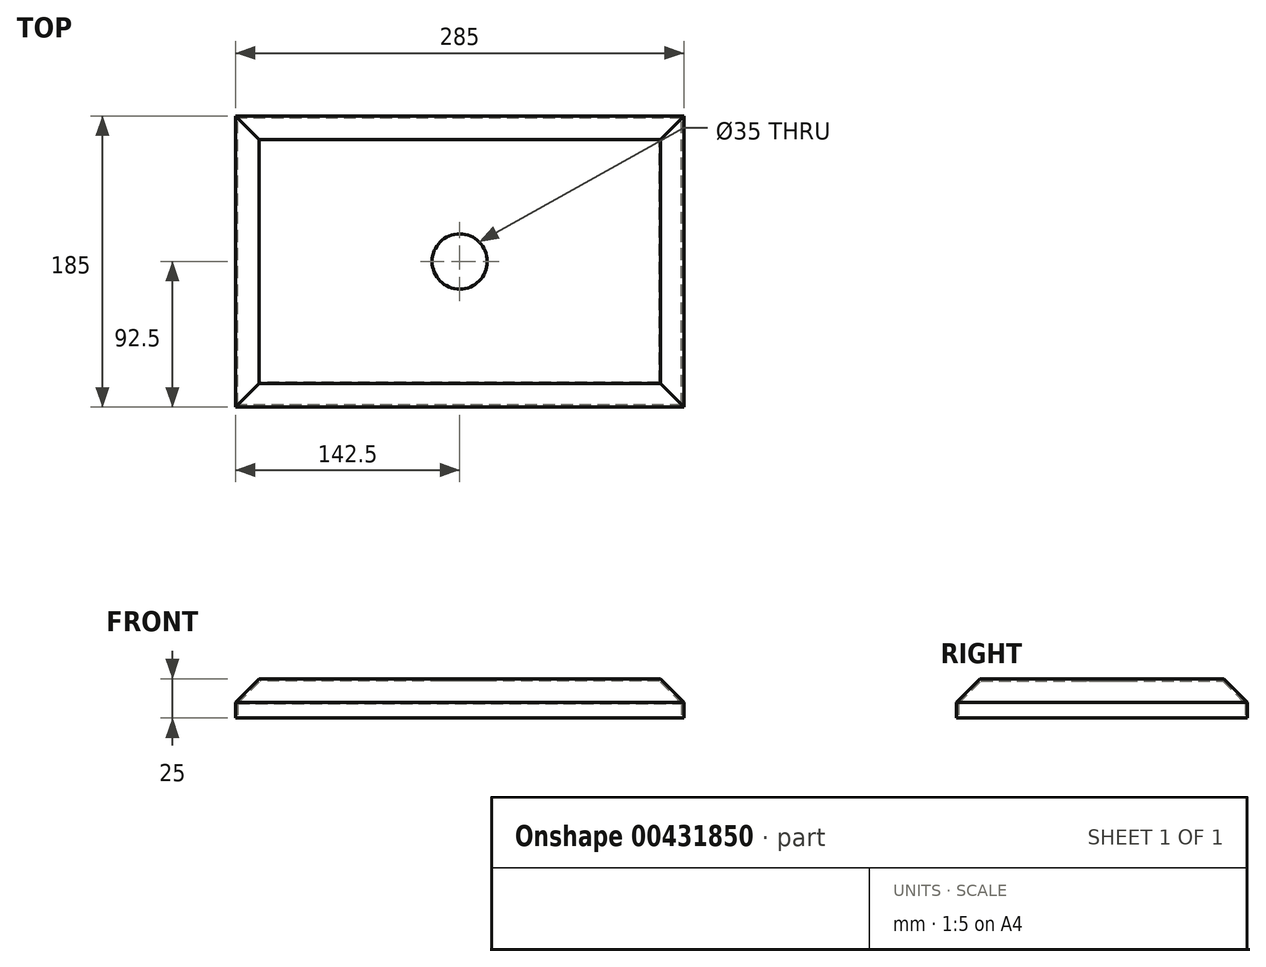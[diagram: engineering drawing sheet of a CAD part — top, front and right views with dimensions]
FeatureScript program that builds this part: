
annotation { "Feature Type Name" : "Feature", "Feature Type Description" : "" }
export const myFeature = defineFeature(function(context is Context, id is Id, definition is map)
    precondition{}
    {
        {
            var Q0;
            Q0=qCreatedBy(makeId("Top.planeOp"),FACE);
            var sketch = newSketch(context, id + "F0", { "sketchPlane" : qUnion([Q0])});
            skLineSegment(sketch, "E0.bottom", {"start": v(0, 0) * mm, "end": v(-285, 0) * mm});
            skLineSegment(sketch, "E0.top", {"start": v(0, 185) * mm, "end": v(-285, 185) * mm});
            skLineSegment(sketch, "E0.left", {"start": v(0, 0) * mm, "end": v(0, 185) * mm});
            skLineSegment(sketch, "E0.right", {"start": v(-285, 0) * mm, "end": v(-285, 185) * mm});
            skPoint(sketch, "E1", {"position": v(-142.5, 92.5) * mm});
            skCircle(sketch, "E2", {"center": v(-142.5, 92.5) * mm, "radius": 17.5 * mm});
            skSolve(sketch);
        }
        {
            var Q0;
            Q0 = qSketchRegion(id + "F0", true);
            extrude(context, id + "F1", {"entities" : qUnion([Q0]), "depth" : 25 * mm});
        }
        {
            var Q0;
            Q0=makeQuery(id+"F1.opExtrude","CAP_EDGE",EDGE,{"disambiguationData":[OSD([sQuery(id+"F0.wireOp",EDGE,"E0.left")])],"isStart":false});
            var Q1;
            Q1=makeQuery(id+"F1.opExtrude","CAP_EDGE",EDGE,{"disambiguationData":[OSD([sQuery(id+"F0.wireOp",EDGE,"E0.top")])],"isStart":false});
            var Q2;
            Q2=makeQuery(id+"F1.opExtrude","CAP_EDGE",EDGE,{"disambiguationData":[OSD([sQuery(id+"F0.wireOp",EDGE,"E0.right")])],"isStart":false});
            var Q3;
            Q3=makeQuery(id+"F1.opExtrude","CAP_EDGE",EDGE,{"disambiguationData":[OSD([sQuery(id+"F0.wireOp",EDGE,"E0.bottom")])],"isStart":false});
            chamfer(context, id + "F2", {"entities" : qUnion([Q0, Q1, Q2, Q3]), "width" : 15 * mm, "tangentPropagation" : true});
        }
        {
            var Q0;
            Q0=makeQuery(id+"F1.opExtrude","CAP_FACE",FACE,{"disambiguationData":[OSD([sQuery(id+"F0.wireOp",EDGE,"E0.bottom"),sQuery(id+"F0.wireOp",EDGE,"E0.top"),sQuery(id+"F0.wireOp",EDGE,"E0.left"),sQuery(id+"F0.wireOp",EDGE,"E0.right")])],"isStart":true});
            var Q1;
            Q1=makeQuery(id+"F1.opExtrude","SWEPT_FACE",FACE,{"disambiguationData":[OSD([sQuery(id+"F0.wireOp",EDGE,"E2")])]});
            shell(context, id + "F3", {"entities" : qUnion([Q0, Q1]), "thickness" : 1.5 * mm});
        }
    });
